# Revit family: ERK9635W_RAD766N
name_source: partatom
category: 照明器具
units: mm (PartAtom-declared; Revit-internal decimal feet)

## family parameters
OmniClass タイトル = Direct/Indirect
OmniClass 番号 = 23.80.70.11.14.17
パーツ タイプ = 標準
ロード時にボイドで切り取り = はい
丸型コネクタ寸法 = 直径を使用
作業面ベース = いいえ
光源 = はい
共有 = いいえ
常に垂直 = はい
部屋計算ポイント = いいえ

## types (1)
- ERK9635W_RAD766N
    Clearance Back = 0  [stored 0 ft]
    Clearance Bottom = 0  [stored 0 ft]
    Clearance Front = 0  [stored 0 ft]
    Clearance Left = 0  [stored 0 ft]
    Clearance Right = 0  [stored 0 ft]
    Clearance Top = 0  [stored 0 ft]
    Depth = 1250  [stored 4.10105 ft]
    Height = 57  [stored 0.187008 ft]
    IfcExportAs = IfcLightFixtureType
    OmniClassCode = 23.80.70.11.14.17
    URL = https://www.endo-lighting.co.jp
    Width = 150
    diameter = 0  [stored 0 ft]
    イメージ(タイプ) = <なし>
    カラー フィルタ = 16777215
    サービススペース表示 = いいえ
    シンボル表示 = はい
    フォトメトリック Web ファイル = ERK9635W_RAD766N.IES
    モデル = ERK9635W_RAD766N
    ランプ = LED
    ランプ_全光束 = 0 lm
    ランプ_定格消費効率(lm/W) = 0
    ランプ_定格消費電力 = 0 W
    ランプ_本数 = 0
    ランプ_電流 = 0 A
    ランプの種類 = LED
    企業コード = 6932
    価格 = 29050 $
    傾斜角 = 90.00°
    公共型番 = LSS9-4-48
    分類コード = 40305100000000
    周波数 = 0 Hz
    呼称 = ベースライト
    固有エネルギー消費効率(lm/W) = 167.4
    埋込穴寸法 = 0
    埋込高さ = 0
    安定器_二次電圧 = 0 V
    安定器_入力電力 = 0 W
    安定器_入力電流 = 0 A
    安定器_定格電圧 = 0 V
    定格光束 = 5173 lm
    定格入力容量 = 0 VA
    定格入力電圧 = 0 V
    定格入力電流 = 0 A
    定格消費電力 = 31 W
    平均演色評価数(Ra) = 82
    形式 = ベースライト
    既定の高さ = 0  [stored 0 ft]
    材質_カバー = <カテゴリ別>
    材質_ルーバー = <カテゴリ別>
    材質_反射板 = <カテゴリ別>
    材質_本体 = <カテゴリ別>
    極数 = 1
    用途 = E_一般照明
    皮相負荷 = 0 VA
    相 = 1
    積算_科目 = 1 電灯設備
    積算_科目2 = [1_1]照明
    製品リリース年月 = 2023.04
    製品質量 = 0.00 kg
    製造元 = 株式会社遠藤照明
    説明 = ベースライト 逆富士 40Wタイプ W+150
    調光ランプの色温度変化。 = <なし>
    負荷分類 = 8_照明
    質量 = 0.00 kg
    運転質量 = 0.00 kg
    電源種別_記号 = AC

note: [stored X ft] marks values corroborated as IEEE doubles in the binary element streams (Revit-internal decimal feet)
